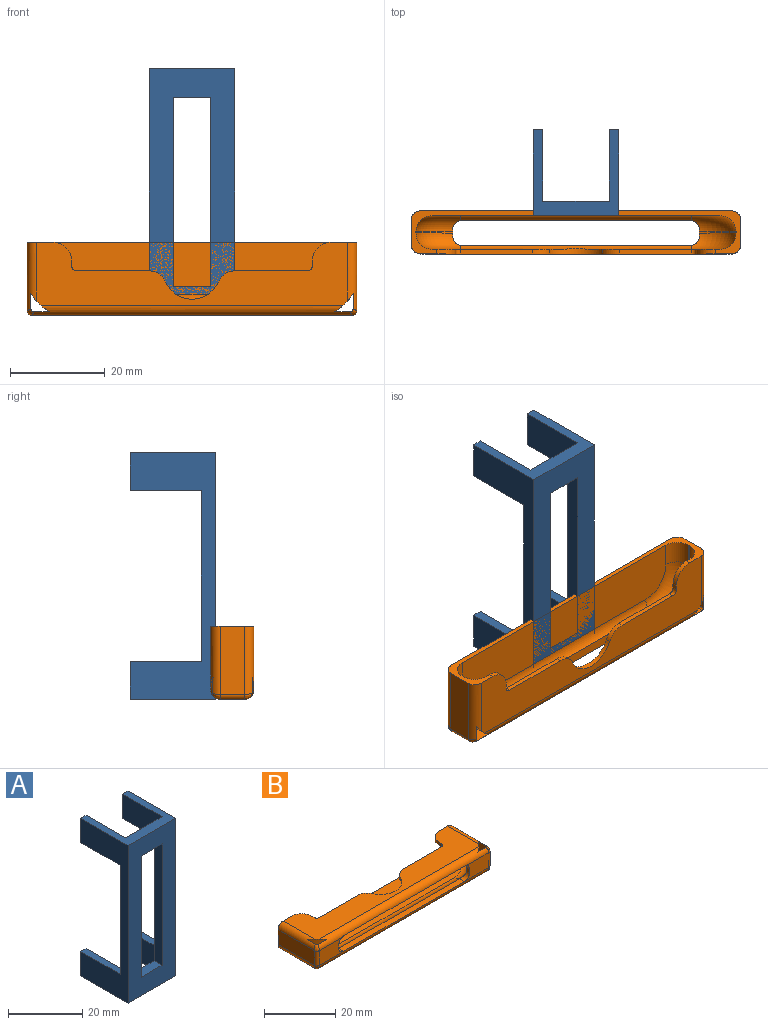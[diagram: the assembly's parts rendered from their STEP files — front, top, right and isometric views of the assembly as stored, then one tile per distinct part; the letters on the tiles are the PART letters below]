
ASSEMBLY  parts=2 mates=2
PART A: 22 faces, bbox 18x18x52 mm
  f0: plane 18x18mm, normal (0,0,1), area 114mm2, adj f1,f7,f8,f9,f11,f12,f14,f15
  f1: plane 52x18mm, normal (-1,0,0), area 396mm2, adj f0,f2,f8,f9,f13,f15,f16,f18
  f2: plane 18x18mm, normal (0,0,-1), area 114mm2, adj f1,f7,f8,f9,f17,f18,f20,f21
  f3: plane 40x3mm, normal (1,0,0), area 120mm2, adj f4,f6,f8,f9
  f4: plane 8x3mm, normal (0,0,-1), area 24mm2, adj f3,f5,f8,f9
  f5: plane 40x3mm, normal (-1,0,0), area 120mm2, adj f4,f6,f8,f9
  f6: plane 8x3mm, normal (0,0,1), area 24mm2, adj f3,f5,f8,f9
  f7: plane 52x18mm, normal (1,0,0), area 396mm2, adj f0,f2,f8,f9,f10,f12,f19,f21
  f8: plane 52x18mm, normal (0,-1,0), area 616mm2, adj f0,f1,f2,f3,f4,f5,f6,f7
  f9: plane 52x18mm, normal (0,1,0), area 552mm2, adj f0,f1,f2,f3,f4,f5,f6,f7
  f10: plane 15x2mm, normal (0,0,-1), area 30mm2, adj f7,f9,f11,f12
  f11: plane 15x8mm, normal (-1,0,0), area 120mm2, adj f0,f9,f10,f12
  f12: plane 8x2mm, normal (0,1,0), area 16mm2, adj f0,f7,f10,f11
  f13: plane 15x2mm, normal (0,0,-1), area 30mm2, adj f1,f9,f14,f15
  f14: plane 15x8mm, normal (1,0,0), area 120mm2, adj f0,f9,f13,f15
  f15: plane 8x2mm, normal (0,1,0), area 16mm2, adj f0,f1,f13,f14
  f16: plane 15x2mm, normal (0,0,1), area 30mm2, adj f1,f9,f17,f18
  f17: plane 15x8mm, normal (1,0,0), area 120mm2, adj f2,f9,f16,f18
  f18: plane 8x2mm, normal (0,1,0), area 16mm2, adj f1,f2,f16,f17
  f19: plane 15x2mm, normal (0,0,1), area 30mm2, adj f7,f9,f20,f21
  f20: plane 15x8mm, normal (-1,0,0), area 120mm2, adj f2,f9,f19,f21
  f21: plane 8x2mm, normal (0,1,0), area 16mm2, adj f2,f7,f19,f20
PART B: 63 faces, bbox 69.5x15.4x9.1 mm
  f0: cylinder r=2mm len=67.5mm, axis (1,0,0), area 194.3mm2, adj f1,f6,f11,f25,f38,f41,f42,f45
  f1: plane 65.5x13.4mm, normal (0,0,1), area 506.2mm2, adj f0,f7,f14,f19,f22,f24,f28,f32
  f2: plane 65.5x13.4mm, normal (0,0,-1), area 876.7mm2, adj f3,f4,f34,f38,f42,f47
  f3: cylinder r=2mm len=67.5mm, axis (-1,0,0), area 204.1mm2, adj f2,f5,f11,f25,f38,f41,f42,f45
  f4: cylinder r=2mm len=14.4mm, axis (0,-1,0), area 41.2mm2, adj f2,f5,f33,f34,f42,f43
  f5: bspline ~1.94x1.47mm, area 2.6mm2, adj f3,f4,f43,f44,f45,f62
  f6: bspline ~1.94x1.47mm, area 2.6mm2, adj f0,f7,f43,f44,f45,f62
  f7: cylinder r=2mm len=14.4mm, axis (0,1,0), area 41.2mm2, adj f1,f6,f33,f34,f42,f43
  f8: cylinder r=9.4mm len=9.25mm, axis (0,0,1), area 3.9mm2, adj f9,f16,f21,f56
  f9: torus R=6mm, axis (0,0,1), area 65.4mm2, adj f8,f10,f17,f18,f56,f57
  f10: cylinder r=3.4mm len=48.7mm, axis (1,0,0), area 111.4mm2, adj f9,f12,f13,f18,f50,f57,f58,f59
  f11: plane 9.75x5.1mm, normal (0,-1,0), area 41mm2, adj f0,f3,f40,f55,f56,f57
  f12: torus R=6mm, axis (0,0,1), area 65.4mm2, adj f10,f13,f27,f31,f59,f60
  f13: plane 27.03x11mm, normal (0,0,-1), area 143.1mm2, adj f10,f12,f24,f28,f31,f32,f34,f36
  f14: plane 15.19x1mm, normal (0,1,0), area 15.2mm2, adj f1,f18,f22,f51
  f15: cylinder r=3.4mm len=5mm, axis (0,-1,0), area 26.5mm2, adj f16,f21,f34,f35
  f16: plane 5x0.3mm, normal (1,0,0), area 1.5mm2, adj f8,f15,f17,f34
  f17: cylinder r=3.4mm len=5mm, axis (0,-1,0), area 27mm2, adj f9,f16,f18,f34
  f18: plane 27.03x11mm, normal (0,0,-1), area 143.1mm2, adj f9,f10,f14,f17,f19,f22,f34,f37
  f19: plane 1x1mm, normal (1,0,0), area 1mm2, adj f1,f18,f22,f37
  f20: plane 14.4x5.1mm, normal (-1,0,0), area 73.4mm2, adj f34,f40,f47,f48
  f21: torus R=6mm, axis (0,0,1), area 64.5mm2, adj f8,f15,f23,f35,f55,f56
  f22: cylinder r=1mm len=1mm, axis (0,0,1), area 1.6mm2, adj f1,f14,f18,f19
  f23: cylinder r=3.4mm len=48.7mm, axis (1,0,0), area 130.3mm2, adj f21,f26,f35,f53,f54,f55
  f24: plane 15.19x1mm, normal (0,1,0), area 15.2mm2, adj f1,f13,f28,f52
  f25: plane 9.75x5.1mm, normal (0,-1,0), area 41mm2, adj f0,f3,f44,f53,f59,f60
  f26: torus R=6mm, axis (0,0,1), area 64.5mm2, adj f23,f27,f29,f35,f53,f60
  f27: cylinder r=9.4mm len=9.25mm, axis (0,0,1), area 3.9mm2, adj f12,f26,f30,f60
  f28: cylinder r=1mm len=1mm, axis (0,0,1), area 1.6mm2, adj f1,f13,f24,f32
  f29: cylinder r=3.4mm len=5mm, axis (0,1,0), area 26.5mm2, adj f26,f30,f34,f35
  f30: plane 5x0.3mm, normal (-1,0,0), area 1.5mm2, adj f27,f29,f31,f34
  f31: cylinder r=3.4mm len=5mm, axis (0,1,0), area 27mm2, adj f12,f13,f30,f34
  f32: plane 1x1mm, normal (-1,0,0), area 1mm2, adj f1,f13,f28,f36
  f33: plane 14.4x5.1mm, normal (1,0,0), area 73.4mm2, adj f4,f7,f34,f44
  f34: plane 69.5x9.1mm, normal (0,1,0), area 101mm2, adj f1,f2,f4,f7,f13,f15,f16,f17
  f35: plane 60.7x11mm, normal (0,0,1), area 652.2mm2, adj f15,f21,f23,f26,f29,f34
  f36: cylinder r=4mm len=4mm, axis (0,0,1), area 6.3mm2, adj f1,f13,f32,f34
  f37: cylinder r=4mm len=4mm, axis (0,0,1), area 6.3mm2, adj f1,f18,f19,f34
  f38: cylinder r=11.2mm len=9.1mm, axis (0,0,1), area 48.2mm2, adj f0,f1,f2,f3,f39,f41,f47,f48
  f39: plane 8.3x3.33mm, normal (1,0,0), area 27.6mm2, adj f38,f46,f47,f48,f49,f61
  f40: cylinder r=1mm len=5.1mm, axis (0,0,1), area 8mm2, adj f11,f20,f46,f49
  f41: plane 8.3x3.33mm, normal (0,1,0), area 27.6mm2, adj f0,f3,f38,f46,f49,f61
  f42: cylinder r=11.2mm len=9.1mm, axis (0,0,1), area 48.2mm2, adj f0,f1,f2,f3,f4,f7,f43,f45
  f43: plane 8.3x3.33mm, normal (-1,0,0), area 27.6mm2, adj f4,f5,f6,f7,f42,f62
  f44: cylinder r=1mm len=5.1mm, axis (0,0,1), area 8mm2, adj f5,f6,f25,f33
  f45: plane 8.3x3.33mm, normal (0,1,0), area 27.6mm2, adj f0,f3,f5,f6,f42,f62
  f46: bspline ~1.94x1.47mm, area 2.6mm2, adj f3,f39,f40,f41,f47,f61
  f47: cylinder r=2mm len=14.4mm, axis (0,1,0), area 41.2mm2, adj f2,f20,f34,f38,f39,f46
  f48: cylinder r=2mm len=14.4mm, axis (0,-1,0), area 41.2mm2, adj f1,f20,f34,f38,f39,f49
  f49: bspline ~1.94x1.47mm, area 2.6mm2, adj f0,f39,f40,f41,f48,f61
  f50: cylinder r=6mm len=11mm, axis (0,0,1), area 13.9mm2, adj f1,f10,f13,f18,f51,f52
  f51: cylinder r=4mm len=3.67mm, axis (0,0,1), area 4.6mm2, adj f1,f14,f18,f50
  f52: cylinder r=4mm len=3.67mm, axis (0,0,1), area 4.6mm2, adj f1,f13,f24,f50
  f53: cylinder r=2mm len=2mm, axis (0,1,0), area 5.1mm2, adj f23,f25,f26,f54,f60
  f54: plane 48x1.99mm, normal (0,0,1), area 95.6mm2, adj f3,f23,f53,f55
  f55: cylinder r=2mm len=2mm, axis (0,1,0), area 5.1mm2, adj f11,f21,f23,f54,f56
  f56: plane 1.3x1.2mm, normal (1,0,0), area 1.5mm2, adj f8,f9,f11,f21,f55,f57
  f57: cylinder r=2mm len=2.21mm, axis (0,1,0), area 5.5mm2, adj f0,f9,f10,f11,f56,f58
  f58: plane 48x2.2mm, normal (0,0,-1), area 105.5mm2, adj f0,f10,f57,f59
  f59: cylinder r=2mm len=2.21mm, axis (0,1,0), area 5.5mm2, adj f0,f10,f12,f25,f58,f60
  f60: plane 1.3x1.2mm, normal (-1,0,0), area 1.5mm2, adj f12,f25,f26,f27,f53,f59
  f61: cylinder r=0.5mm len=8.29mm, axis (0,0,1), area 6.5mm2, adj f39,f41,f46,f49
  f62: cylinder r=0.5mm len=8.29mm, axis (0,0,1), area 6.5mm2, adj f5,f6,f43,f45
PLACE A t=(0,0,16)mm
PLACE B rot(axis=(1,0,0),90deg) t=(0,-2,-5.6)mm
MATE planar B.f11 <-> A.f2  axis (0,0,-1) through (-29.73,-6.54,-10)mm
MATE planar B.f35 <-> A.f8  axis (0,-1,0) through (0,-3,0)mm
